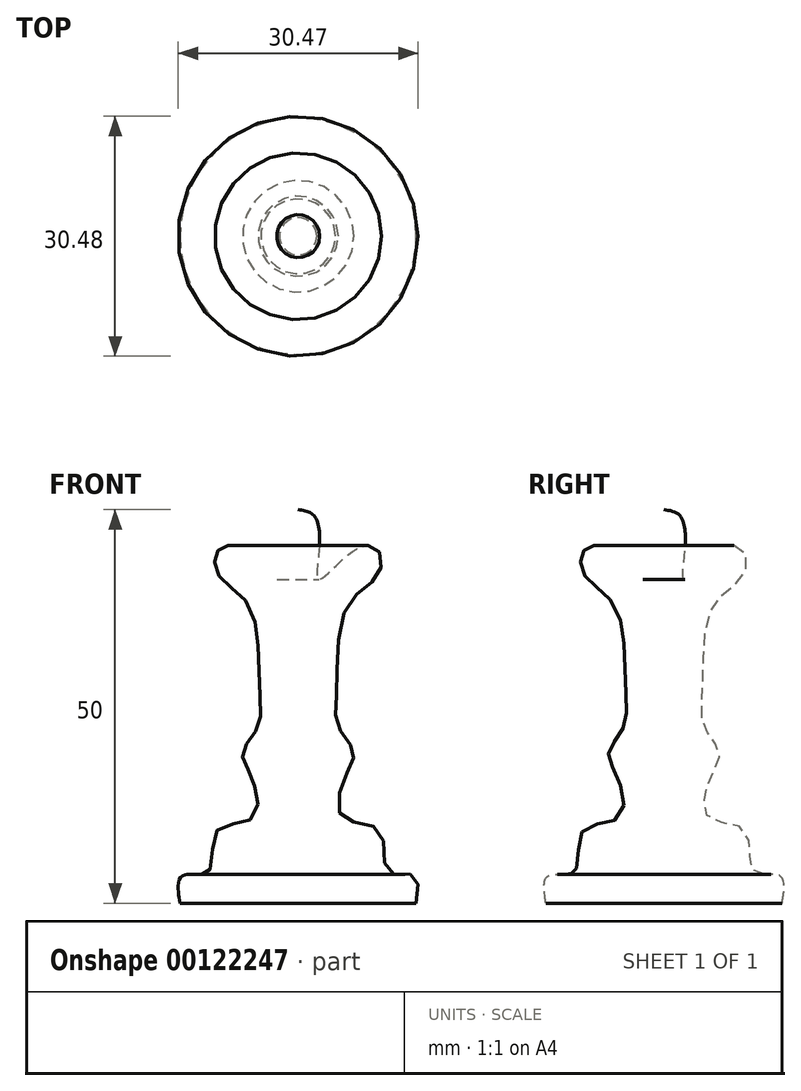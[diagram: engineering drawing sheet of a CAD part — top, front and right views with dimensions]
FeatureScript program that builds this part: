
annotation { "Feature Type Name" : "Feature", "Feature Type Description" : "" }
export const myFeature = defineFeature(function(context is Context, id is Id, definition is map)
    precondition{}
    {
        {
            var Q0;
            Q0=qCreatedBy(makeId("Front.planeOp"),FACE);
            var sketch = newSketch(context, id + "F0", { "sketchPlane" : qUnion([Q0])});
            skLineSegment(sketch, "E0", {"start": v(24.63, -22.38) * mm, "end": v(9.63, -22.38) * mm});
            skLineSegment(sketch, "E1", {"start": v(9.63, -22.38) * mm, "end": v(9.63, 27.62) * mm});
            skFitSpline(sketch, "E2", {"points": [v(9.63, 27.62) * mm, v(11.7, 26.81) * mm, v(12.26, 21.93) * mm, v(12.26, 18.74) * mm, v(16.8, 22.5) * mm, v(19.76, 22.5) * mm, v(19.76, 19.31) * mm, v(15.9, 15.45) * mm, v(14.54, 5) * mm, v(14.76, 0) * mm, v(16.7, -3.2) * mm, v(15.56, -6.37) * mm, v(15.33, -11.49) * mm, v(20, -13.2) * mm, v(21.01, -18.3) * mm, v(24.3, -18.87) * mm, v(24.63, -22.38) * mm], "startDerivative": vector(53.27, -6.74) * mm, "endDerivative": vector(-13.12, -81.96) * mm});
            skSolve(sketch);
        }
        {
            var Q0;
            Q0=makeQuery(id+"F0.imprint","IMPRINT",FACE,{"disambiguationData":[TD([[makeQuery(id+"F0.imprint","IMPRINT",EDGE,{"derivedFrom":sQuery(id+"F0.wireOp",EDGE,"E0")}),-1.0]])]});
            var Q1;
            Q1=sQuery(id+"F0.wireOp",EDGE,"E1");
            revolve(context, id + "F1", {"entities" : qUnion([Q0]), "axis" : qUnion([Q1]), "revolveType" : RevolveType.FULL});
        }
    });
